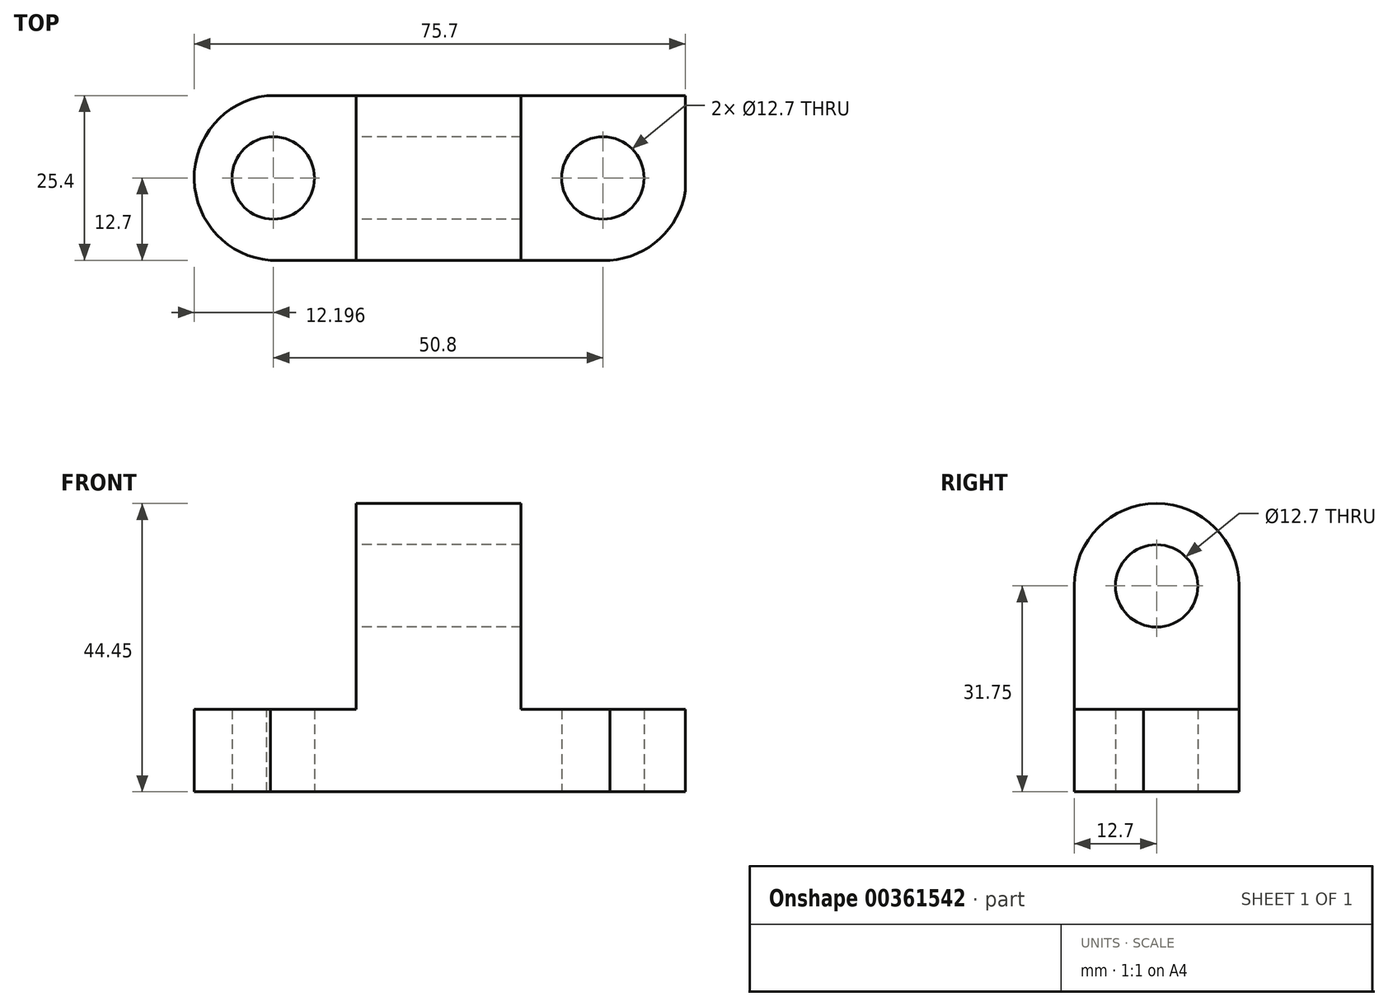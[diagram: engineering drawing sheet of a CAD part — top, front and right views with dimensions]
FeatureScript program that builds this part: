
annotation { "Feature Type Name" : "Feature", "Feature Type Description" : "" }
export const myFeature = defineFeature(function(context is Context, id is Id, definition is map)
    precondition{}
    {
        {
            var Q0;
            Q0=qCreatedBy(makeId("Top.planeOp"),FACE);
            var sketch = newSketch(context, id + "F0", { "sketchPlane" : qUnion([Q0])});
            skLineSegment(sketch, "E0.bottom", {"start": v(-31.77, 25.4) * mm, "end": v(44.43, 25.4) * mm});
            skLineSegment(sketch, "E0.top", {"start": v(-31.77, 0) * mm, "end": v(44.43, 0) * mm});
            skLineSegment(sketch, "E0.left", {"start": v(-31.77, 25.4) * mm, "end": v(-31.77, 0) * mm});
            skLineSegment(sketch, "E0.right", {"start": v(44.43, 25.4) * mm, "end": v(44.43, 0) * mm});
            skCircle(sketch, "E1", {"center": v(-19.07, 12.7) * mm, "radius": 6.35 * mm});
            skPoint(sketch, "E1.centerSnap0", {"position": v(-31.77, 12.7) * mm});
            skCircle(sketch, "E2", {"center": v(31.73, 12.7) * mm, "radius": 6.35 * mm});
            skSolve(sketch);
        }
        {
            var Q0;
            Q0 = qSketchRegion(id + "F0", true);
            extrude(context, id + "F1", {"entities" : qUnion([Q0]), "depth" : 12.7 * mm});
        }
        {
            var Q0;
            Q0=makeQuery(id+"F1.opExtrude","CAP_FACE",FACE,{"disambiguationData":[OSD([sQuery(id+"F0.wireOp",EDGE,"E0.bottom"),sQuery(id+"F0.wireOp",EDGE,"E0.top"),sQuery(id+"F0.wireOp",EDGE,"E0.left"),sQuery(id+"F0.wireOp",EDGE,"E0.right"),sQuery(id+"F0.wireOp",EDGE,"E1"),sQuery(id+"F0.wireOp",EDGE,"E2")])],"isStart":false});
            var sketch = newSketch(context, id + "F2", { "sketchPlane" : qUnion([Q0])});
            skArc(sketch, "E3", {"start": v(-20.12, 25.4) * mm, "mid": v(-31.26, 12.42) * mm, "end": v(-19.5, 0) * mm});
            skArc(sketch, "E4", {"start": v(32.8, 0) * mm, "mid": v(44.55, 13.63) * mm, "end": v(30.95, 25.4) * mm});
            skSolve(sketch);
        }
        {
            var Q0;
            {var subQ0=sQuery(id+"F2.wireOp",EDGE,"E3");Q0=makeQuery(id+"F2.imprint","IMPRINT",FACE,{"disambiguationData":[TD([[makeQuery(id+"F2.imprint","IMPRINT",EDGE,{"derivedFrom":subQ0}),-1.0]])]});}
            var Q1;
            {var subQ0=sQuery(id+"F2.wireOp",EDGE,"E4");var subQ1=makeQuery(id+"F1.opExtrude","CAP_EDGE",EDGE,{"disambiguationData":[OSD([sQuery(id+"F0.wireOp",EDGE,"E0.right")])],"isStart":false});var subQ2=makeQuery(id+"F2.imprint","INTERSECT",VERTEX,{"disambiguationData":[OD(1.0)],"derivedFrom":[subQ1,subQ0]});Q1=makeQuery(id+"F2.imprint","IMPRINT",FACE,{"disambiguationData":[TD([[makeQuery(id+"F2.imprint","IMPRINT",EDGE,{"disambiguationData":[TD([[subQ2,-1.0]])],"derivedFrom":subQ0}),-1.0]])]});}
            var Q2;
            {var subQ0=sQuery(id+"F2.wireOp",EDGE,"E4");var subQ1=makeQuery(id+"F1.opExtrude","CAP_EDGE",EDGE,{"disambiguationData":[OSD([sQuery(id+"F0.wireOp",EDGE,"E0.top")])],"isStart":false});var subQ2=makeQuery(id+"F2.imprint","INTERSECT",VERTEX,{"derivedFrom":[subQ1,subQ0]});Q2=makeQuery(id+"F2.imprint","IMPRINT",FACE,{"disambiguationData":[TD([[makeQuery(id+"F2.imprint","IMPRINT",EDGE,{"disambiguationData":[TD([[subQ2,-1.0]])],"derivedFrom":subQ0}),-1.0]])]});}
            extrude(context, id + "F3", {"entities" : qUnion([Q0, Q1, Q2]), "operationType" : NewBodyOperationType.REMOVE, "oppositeDirection" : true, "depth" : 12.7 * mm});
        }
        {
            var Q0;
            Q0=qCreatedBy(makeId("Top.planeOp"),FACE);
            var sketch = newSketch(context, id + "F4", { "sketchPlane" : qUnion([Q0])});
            skLineSegment(sketch, "E5", {"start": v(-6.29, 25.4) * mm, "end": v(-6.29, 0) * mm});
            skLineSegment(sketch, "E6", {"start": v(-6.29, 0) * mm, "end": v(19.11, 0) * mm});
            skLineSegment(sketch, "E7", {"start": v(19.11, 0) * mm, "end": v(19.11, 25.4) * mm});
            skLineSegment(sketch, "E8", {"start": v(19.11, 25.4) * mm, "end": v(-6.29, 25.4) * mm});
            skSolve(sketch);
        }
        {
            var Q0;
            Q0 = qSketchRegion(id + "F4", true);
            extrude(context, id + "F5", {"entities" : qUnion([Q0]), "operationType" : NewBodyOperationType.ADD, "depth" : 44.45 * mm});
        }
        {
            var Q0;
            Q0=makeQuery(id+"F5.opExtrude","SWEPT_FACE",FACE,{"disambiguationData":[OSD([sQuery(id+"F4.wireOp",EDGE,"E5")])]});
            var sketch = newSketch(context, id + "F6", { "sketchPlane" : qUnion([Q0])});
            skCircle(sketch, "E9", {"center": v(-12.7, 31.75) * mm, "radius": 12.7 * mm});
            skPoint(sketch, "E9.first.point", {"position": v(-25.4, 31.75) * mm});
            skPoint(sketch, "E9.second.point", {"position": v(0, 31.75) * mm});
            skPoint(sketch, "E9.third.point", {"position": v(-12.7, 44.45) * mm});
            skSolve(sketch);
        }
        {
            var Q0;
            {var subQ0=sQuery(id+"F6.wireOp",EDGE,"E9");var subQ1=sQuery(id+"F4.wireOp",EDGE,"E5");var subQ2=makeQuery(id+"F5.opExtrude","CAP_EDGE",EDGE,{"disambiguationData":[OSD([subQ1])],"isStart":false});var subQ3=makeQuery(id+"F6.imprint","INTERSECT",VERTEX,{"derivedFrom":[subQ2,subQ0]});Q0=makeQuery(id+"F6.imprint","IMPRINT",FACE,{"disambiguationData":[TD([[makeQuery(id+"F6.imprint","IMPRINT",EDGE,{"disambiguationData":[TD([[subQ3,-1.0]])],"derivedFrom":subQ0}),-1.0]])]});}
            var Q1;
            {var subQ0=sQuery(id+"F6.wireOp",EDGE,"E9");var subQ1=sQuery(id+"F4.wireOp",EDGE,"E5");var subQ2=makeQuery(id+"F5.opExtrude","CAP_EDGE",EDGE,{"disambiguationData":[OSD([subQ1])],"isStart":false});var subQ3=makeQuery(id+"F6.imprint","INTERSECT",VERTEX,{"derivedFrom":[subQ2,subQ0]});Q1=makeQuery(id+"F6.imprint","IMPRINT",FACE,{"disambiguationData":[TD([[makeQuery(id+"F6.imprint","IMPRINT",EDGE,{"disambiguationData":[TD([[subQ3,1.0]])],"derivedFrom":subQ0}),-1.0]])]});}
            extrude(context, id + "F7", {"entities" : qUnion([Q0, Q1]), "operationType" : NewBodyOperationType.REMOVE, "oppositeDirection" : true, "depth" : 25.4 * mm});
        }
        {
            var Q0;
            Q0=makeQuery(id+"F5.opExtrude","SWEPT_FACE",FACE,{"disambiguationData":[OSD([sQuery(id+"F4.wireOp",EDGE,"E5")])]});
            var sketch = newSketch(context, id + "F8", { "sketchPlane" : qUnion([Q0])});
            skCircle(sketch, "E10", {"center": v(-12.7, 31.75) * mm, "radius": 6.35 * mm});
            skSolve(sketch);
        }
        {
            var Q0;
            Q0=makeQuery(id+"F8.imprint","IMPRINT",FACE,{"disambiguationData":[TD([[makeQuery(id+"F8.imprint","IMPRINT",EDGE,{"derivedFrom":sQuery(id+"F8.wireOp",EDGE,"E10")}),1.0]])]});
            extrude(context, id + "F9", {"entities" : qUnion([Q0]), "operationType" : NewBodyOperationType.REMOVE, "oppositeDirection" : true, "depth" : 25.4 * mm});
        }
    });
